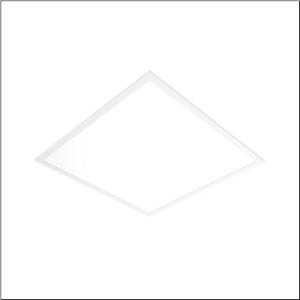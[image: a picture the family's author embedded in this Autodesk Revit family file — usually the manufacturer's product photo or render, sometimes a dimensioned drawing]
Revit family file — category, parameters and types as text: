
# Revit family: apollon_r__41_51mh11w72m43_60bb
name_source: partatom
category: Lighting Fixtures
units: mm (PartAtom-declared; Revit-internal decimal feet)

## family parameters
Cut with Voids When Loaded = No
Host = Face
Light Source = No
Part Type = Normal
Room Calculation Point = No
Round Connector Dimension = Use Diameter
Shared = No

## types (1)
- --- (1 x LED, 3700 lm, 28.5 W, 4000K)
    Apparent Load = 29 VA
    CIE Flux Codes = 61 87 97 100 100
    Color Rendering = 80
    Color Temperature = 4000K
    Default Elevation = 1800 mm
    Description = Apollon® 41, office luminaire, primary optical cover: prismatic diffuser, of PS, light emission: direct distribution, primary light characteristic: symmetric, installation type: lay-in mounting, LED, rated luminous flux: 3.700lm, luminous efficacy: 130lm/W, light colour: 830/840, colour temperature: 3000/4000K, with terminal, 3-pole, mains connection: 220..240V, AC, 50/60Hz, housing, of aluminium section, traffic white (RAL 9016), module: M625, length: 620mm, width: 620mm, height: 28mm, housing upper side, of sheet steel, protection rating (complete): IP20, protection rating (lamp compartment, on room side): IP40, insulation class (complete): insulation class II (safety insulation), certification: CE, ENEC, permissible operating ambient temperature: -25..+40°C, packaging unit: 1 piece
    Height = 0 mm  [stored 0 ft]
    Lamp = 1 x LED
    Lamp Light Flux = 3700 lm
    Lamp Power = 28.5 W
    Lamp count = 1
    Length = 620 mm
    Luminous efficacy = 130 lm/W
    Manufacturer = Siteco
    ModVariant = No
    Model = 51MH11W72M43
    Mounting Place = Ceiling
    Mounting Type = Recessed
    Number of Poles = 1
    OnlyDefault = Yes
    Power Factor = 1
    Product Name = Apollon® 41
    Product group = office luminaire | ceiling recessed
    ProductGroupID = 401
    Protection Class = Protection class II
    Protection Degree = IP 20
    RLX_Detail_Level = 1
    RLX_Emergency_Light_Flux = 0 lm
    RLX_Emergency_Type = 0
    RLX_Emergency_Type_DB = No
    RlxData = <blob elided: 12397 chars, md5=0f994928>
    Socket = socket
    Standby Power = 0 W
    System Light Flux = 3700 lm
    System Power = 29 W
    Type Comments = factory setting
    Type Image = l_1291024.jpg
    URL = http://relux.com
    VarID = @adj_027751
    Voltage = 0 V
    Weight = 0.00 kg
    Width = 620 mm

note: [stored X ft] marks values corroborated as IEEE doubles in the binary element streams (Revit-internal decimal feet)

## geometry (parser evidence)
native form markers: Sweep x9
no freeform markers — native parametric forms only
